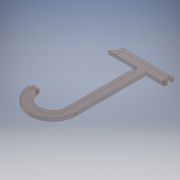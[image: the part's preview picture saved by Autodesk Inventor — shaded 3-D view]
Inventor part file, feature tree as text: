
AUTODESK INVENTOR PART (.ipt)
format: ipt  version: 2017 (Build 210142000, 142)  size: 141,824 bytes
history: native  units: mm
features: extrude x1, sketch x1
ambient origin geometry x8: Origin, YZ Plane, XZ Plane, XY Plane, X Axis, Y Axis, Z Axis, Center Point
bodies: Solid1 (feature_tree)
feature tree (2):
  extrude  "Extrusion1"  Depth=24.990566mm
  sketch  "Sketch1"  dims[d5=5.0mm d7=50.0mm d8=25.0mm d9=15.0mm d10=15.0mm d11=3.17mm d12=0.0mm d16=37.5mm d17=10.0mm d18=75.0mm d20=3.0mm d22=3.0mm d25=60.0deg d26=60.0deg d28=75.0mm d29=90.0deg d31=10.0mm d32=45.0deg d33=5.0mm d39=3.0mm d41=3.0mm d42=60.0deg d43=60.0deg d45=3.0mm d46=19.989518mm d47=24.990566mm d48=45.838996mm]
